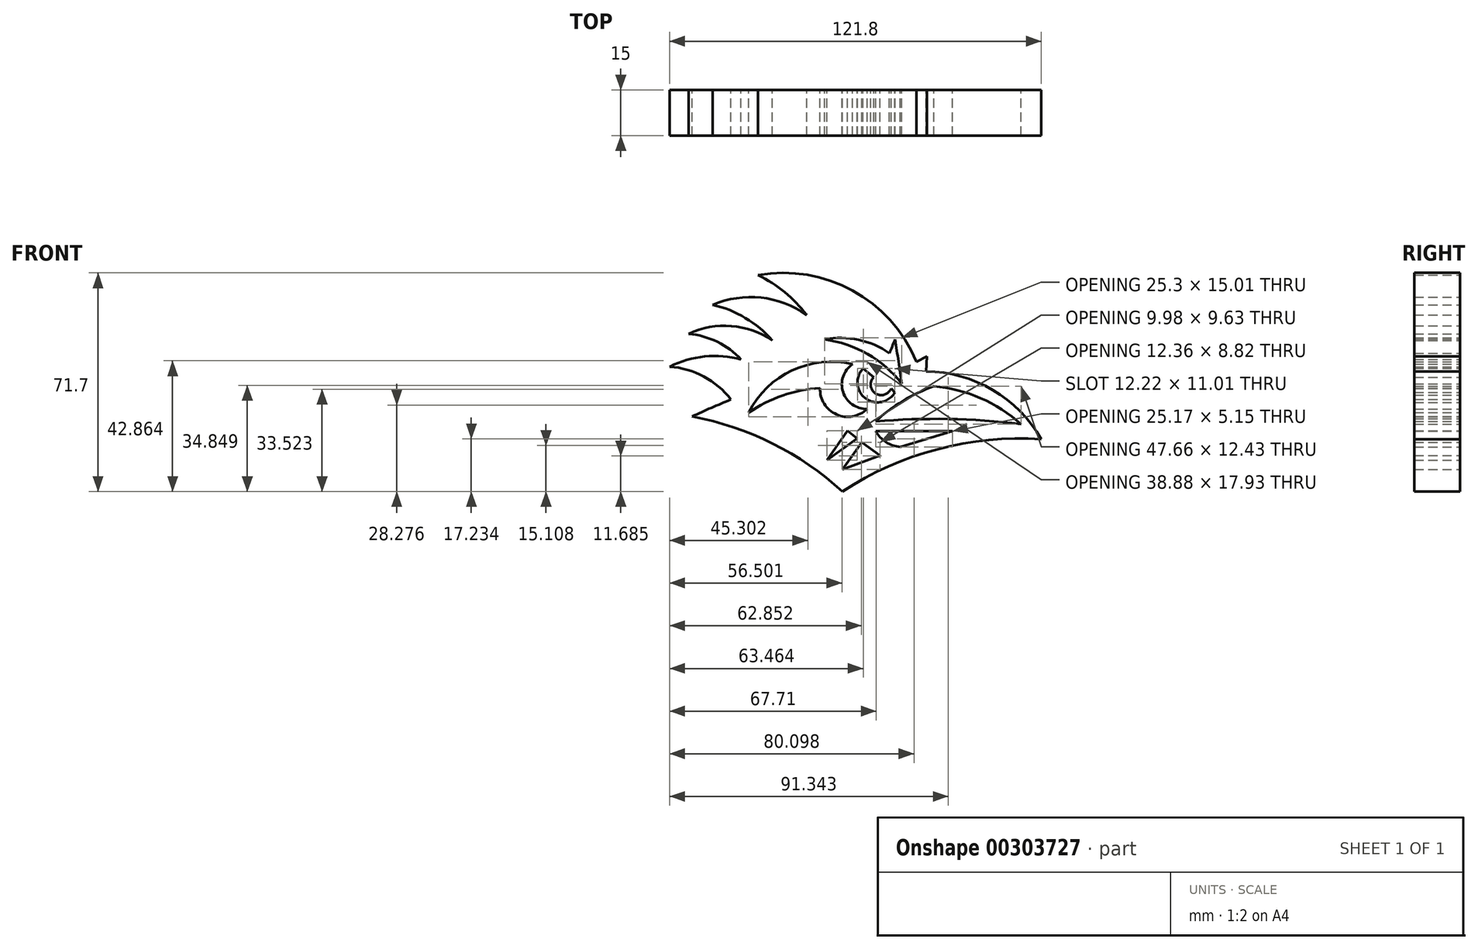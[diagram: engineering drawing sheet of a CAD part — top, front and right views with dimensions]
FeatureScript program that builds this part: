
annotation { "Feature Type Name" : "Feature", "Feature Type Description" : "" }
export const myFeature = defineFeature(function(context is Context, id is Id, definition is map)
    precondition{}
    {
        {
            var Q0;
            Q0=qCreatedBy(makeId("Front.planeOp"),FACE);
            var sketch = newSketch(context, id + "F0", { "sketchPlane" : qUnion([Q0])});
            skArc(sketch, "E0", {"start": v(65.13, -9.92) * mm, "mid": v(49.27, 6.23) * mm, "end": v(27.45, 12.26) * mm});
            skArc(sketch, "E1", {"start": v(65.13, -9.92) * mm, "mid": v(31.17, -13.2) * mm, "end": v(0, -27.09) * mm});
            skArc(sketch, "E2", {"start": v(0, -27.09) * mm, "mid": v(-22.96, -11.36) * mm, "end": v(-49.34, -2.5) * mm});
            skArc(sketch, "E3", {"start": v(-36.58, 3.1) * mm, "mid": v(-42.99, 0.37) * mm, "end": v(-49.34, -2.5) * mm});
            skArc(sketch, "E4", {"start": v(-36.58, 3.1) * mm, "mid": v(-45.47, 10.62) * mm, "end": v(-56.67, 13.85) * mm});
            skArc(sketch, "E5", {"start": v(-33.24, 16.18) * mm, "mid": v(-45.18, 17.2) * mm, "end": v(-56.67, 13.85) * mm});
            skArc(sketch, "E6", {"start": v(-33.24, 16.18) * mm, "mid": v(-41.04, 22) * mm, "end": v(-50.42, 24.6) * mm});
            skArc(sketch, "E7", {"start": v(-23, 22.43) * mm, "mid": v(-36.41, 27.19) * mm, "end": v(-50.42, 24.6) * mm});
            skArc(sketch, "E8", {"start": v(-23, 22.43) * mm, "mid": v(-31.84, 29.85) * mm, "end": v(-42.58, 34.1) * mm});
            skArc(sketch, "E9", {"start": v(-11.74, 30.77) * mm, "mid": v(-26.72, 36.5) * mm, "end": v(-42.58, 34.1) * mm});
            skArc(sketch, "E10", {"start": v(-11.74, 30.77) * mm, "mid": v(-18.91, 38.27) * mm, "end": v(-27.66, 43.86) * mm});
            skArc(sketch, "E11", {"start": v(24.2, 15.51) * mm, "mid": v(3.28, 38.84) * mm, "end": v(-27.66, 43.86) * mm});
            skLineSegment(sketch, "E12", {"start": v(24.2, 15.51) * mm, "end": v(27.62, 17.26) * mm});
            skLineSegment(sketch, "E13", {"start": v(27.62, 17.26) * mm, "end": v(27.45, 12.26) * mm});
            skArc(sketch, "E14", {"start": v(19.44, 8.27) * mm, "mid": v(8.22, 18) * mm, "end": v(-5.86, 22.77) * mm});
            skArc(sketch, "E15", {"start": v(15.38, 18.25) * mm, "mid": v(5.22, 22.67) * mm, "end": v(-5.86, 22.77) * mm});
            skArc(sketch, "E16", {"start": v(17.24, 22.77) * mm, "mid": v(16.3, 20.51) * mm, "end": v(15.38, 18.25) * mm});
            skArc(sketch, "E17", {"start": v(19.44, 8.27) * mm, "mid": v(18.36, 15.52) * mm, "end": v(17.24, 22.77) * mm});
            skArc(sketch, "E18", {"start": v(3.31, 14.65) * mm, "mid": v(-16.5, 12.62) * mm, "end": v(-30.8, -1.25) * mm});
            skArc(sketch, "E19", {"start": v(-7.36, 6.88) * mm, "mid": v(-19.64, 4.4) * mm, "end": v(-30.8, -1.25) * mm});
            skArc(sketch, "E20", {"start": v(-7.36, 6.88) * mm, "mid": v(-1.99, -1.81) * mm, "end": v(8.07, 0) * mm});
            skArc(sketch, "E21", {"start": v(3.31, 14.65) * mm, "mid": v(0.18, 5.54) * mm, "end": v(8.07, 0) * mm});
            skLineSegment(sketch, "E22", {"start": v(1.57, -7.17) * mm, "end": v(4.82, -9.72) * mm});
            skLineSegment(sketch, "E23", {"start": v(4.82, -9.72) * mm, "end": v(-5.16, -16.8) * mm});
            skLineSegment(sketch, "E24", {"start": v(-5.16, -16.8) * mm, "end": v(1.57, -7.17) * mm});
            skLineSegment(sketch, "E25", {"start": v(6.33, -11) * mm, "end": v(12.36, -15.29) * mm});
            skLineSegment(sketch, "E26", {"start": v(12.36, -15.29) * mm, "end": v(0, -19.82) * mm});
            skLineSegment(sketch, "E27", {"start": v(0, -19.82) * mm, "end": v(6.33, -11) * mm});
            skArc(sketch, "E28", {"start": v(10.25, 10.42) * mm, "mid": v(10.8, 5.08) * mm, "end": v(15.92, 6.72) * mm});
            skArc(sketch, "E29", {"start": v(6.74, 13.26) * mm, "mid": v(7.51, 3.47) * mm, "end": v(17.15, 5.36) * mm});
            skLineSegment(sketch, "E30", {"start": v(6.74, 13.26) * mm, "end": v(10.25, 10.42) * mm});
            skLineSegment(sketch, "E31", {"start": v(15.92, 6.72) * mm, "end": v(17.15, 5.36) * mm});
            skArc(sketch, "E32", {"start": v(29.92, 7.4) * mm, "mid": v(19.78, 2.63) * mm, "end": v(10.84, -4.13) * mm});
            skArc(sketch, "E33", {"start": v(58.5, -5.03) * mm, "mid": v(45.24, 3.56) * mm, "end": v(29.92, 7.4) * mm});
            skArc(sketch, "E34", {"start": v(58.5, -5.03) * mm, "mid": v(34.7, -3.32) * mm, "end": v(10.84, -4.13) * mm});
            skArc(sketch, "E35", {"start": v(10.84, -7.28) * mm, "mid": v(14.24, -10.86) * mm, "end": v(18.9, -12.43) * mm});
            skLineSegment(sketch, "E36", {"start": v(10.84, -7.28) * mm, "end": v(36.01, -7.28) * mm});
            skLineSegment(sketch, "E37", {"start": v(36.01, -7.28) * mm, "end": v(18.9, -12.43) * mm});
            skSolve(sketch);
        }
        {
            var Q0;
            Q0 = qSketchRegion(id + "F0", true);
            extrude(context, id + "F1", {"entities" : qUnion([Q0]), "offsetDistance" : 25 * mm, "depth" : 15 * mm});
        }
        {
            var Q0;
            Q0 = qSketchRegion(id + "F0", true);
            extrude(context, id + "F2", {"entities" : qUnion([Q0]), "operationType" : NewBodyOperationType.ADD, "depth" : 3 * mm});
        }
        {
            var Q0;
            Q0 = qSketchRegion(id + "F0", true);
            extrude(context, id + "F3", {"entities" : qUnion([Q0]), "operationType" : NewBodyOperationType.ADD, "depth" : 3 * mm});
        }
    });
